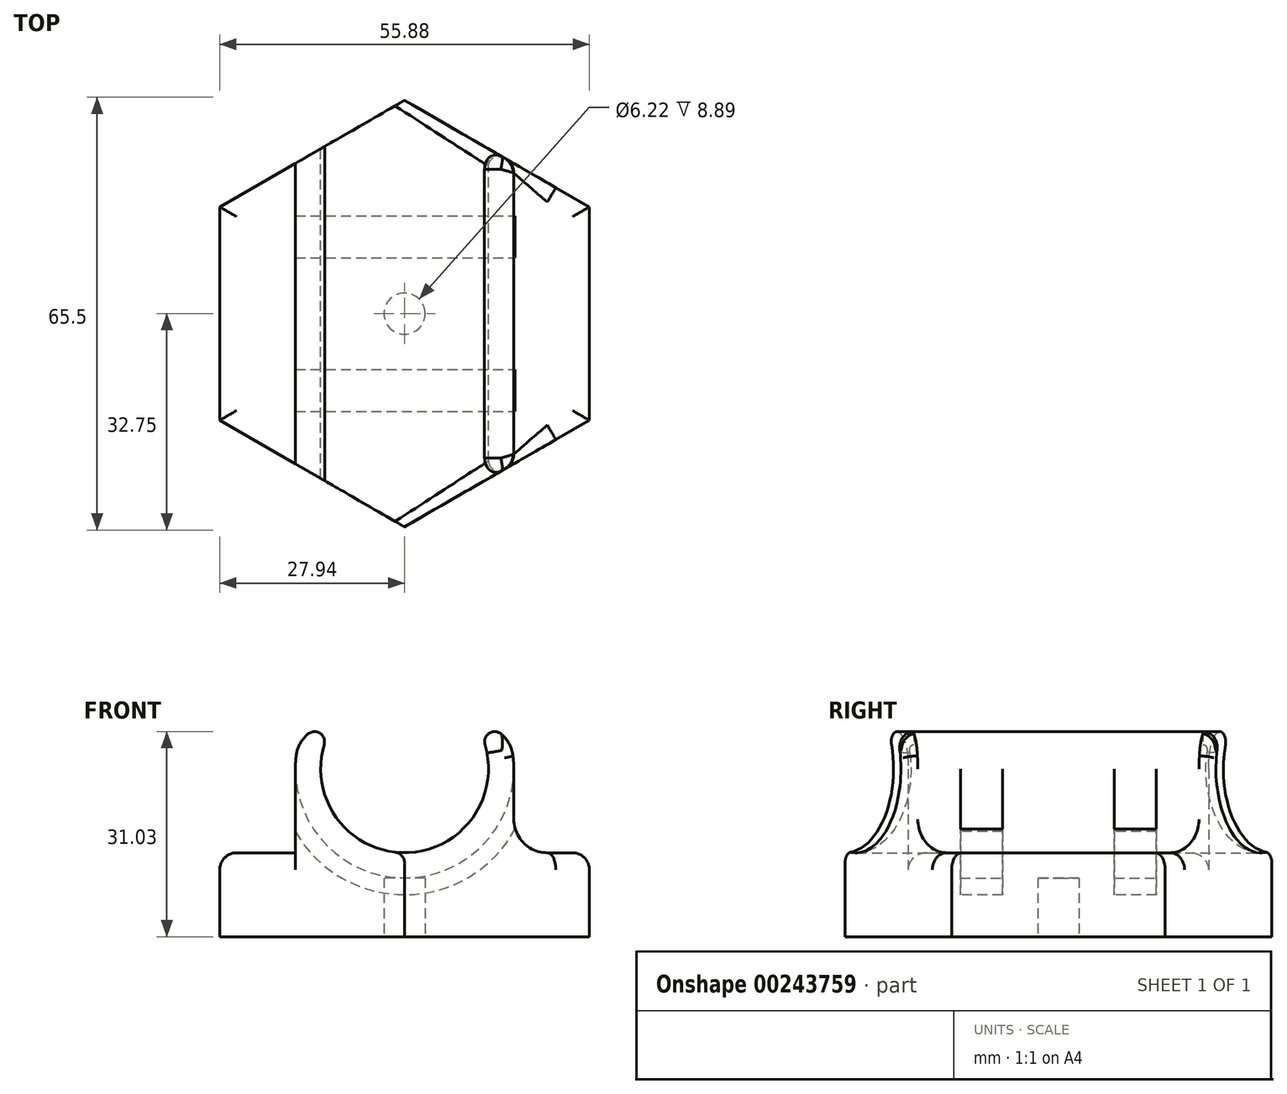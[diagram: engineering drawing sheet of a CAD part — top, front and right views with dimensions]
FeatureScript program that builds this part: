
annotation { "Feature Type Name" : "Feature", "Feature Type Description" : "" }
export const myFeature = defineFeature(function(context is Context, id is Id, definition is map)
    precondition{}
    {
        {
            var Q0;
            Q0=qCreatedBy(makeId("Top.planeOp"),FACE);
            var sketch = newSketch(context, id + "F0", { "sketchPlane" : qUnion([Q0])});
            skLineSegment(sketch, "E0", {"start": v(0, 0) * mm, "end": v(27.94, 0) * mm});
            skCircle(sketch, "E1.cCircle", {"center": v(0, 0) * mm, "radius": 27.94 * mm, "construction": true});
            skLineSegment(sketch, "E1.0", {"start": v(27.94, 16.13) * mm, "end": v(27.94, -16.13) * mm});
            skLineSegment(sketch, "E1.1", {"start": v(27.94, -16.13) * mm, "end": v(0, -32.26) * mm});
            skLineSegment(sketch, "E1.2", {"start": v(0, -32.26) * mm, "end": v(-27.94, -16.13) * mm});
            skLineSegment(sketch, "E1.3", {"start": v(-27.94, -16.13) * mm, "end": v(-27.94, 16.13) * mm});
            skLineSegment(sketch, "E1.4", {"start": v(-27.94, 16.13) * mm, "end": v(0, 32.26) * mm});
            skLineSegment(sketch, "E1.5", {"start": v(0, 32.26) * mm, "end": v(27.94, 16.13) * mm});
            skPoint(sketch, "E1.0.midPoint", {"position": v(27.94, 0) * mm});
            skCircle(sketch, "E2", {"center": v(0, 0) * mm, "radius": 3.11 * mm});
            skSolve(sketch);
        }
        {
            var Q0;
            {var subQ0=sQuery(id+"F0.wireOp",EDGE,"E1.1");Q0=makeQuery(id+"F0.imprint","IMPRINT",FACE,{"disambiguationData":[TD([[makeQuery(id+"F0.imprint","IMPRINT",EDGE,{"derivedFrom":subQ0}),-1.0]])]});}
            extrude(context, id + "F1", {"entities" : qUnion([Q0]), "depth" : 12.7 * mm});
        }
        {
            var Q0;
            Q0=qCreatedBy(makeId("Front.planeOp"),FACE);
            var sketch = newSketch(context, id + "F2", { "sketchPlane" : qUnion([Q0])});
            skLineSegment(sketch, "E3", {"start": v(0, 0) * mm, "end": v(0, 25.4) * mm});
            skCircle(sketch, "E4", {"center": v(0, 25.4) * mm, "radius": 12.7 * mm});
            skCircle(sketch, "E5", {"center": v(0, 25.4) * mm, "radius": 16.51 * mm});
            skLineSegment(sketch, "E6", {"start": v(0, 0) * mm, "end": v(0, 12.7) * mm});
            skLineSegment(sketch, "E7", {"start": v(0, 12.7) * mm, "end": v(27.94, 12.7) * mm});
            skLineSegment(sketch, "E8", {"start": v(0, 12.7) * mm, "end": v(-27.94, 12.7) * mm});
            skLineSegment(sketch, "E9", {"start": v(-16.51, 25.4) * mm, "end": v(-16.51, 12.7) * mm});
            skLineSegment(sketch, "E10", {"start": v(16.51, 25.4) * mm, "end": v(16.51, 12.7) * mm});
            skLineSegment(sketch, "E11", {"start": v(0, 25.4) * mm, "end": v(-14.24, 33.76) * mm});
            skLineSegment(sketch, "E12", {"start": v(0, 25.4) * mm, "end": v(14.24, 33.76) * mm});
            skSolve(sketch);
        }
        {
            var Q0;
            Q0=makeQuery(id+"F0.imprint","IMPRINT",FACE,{"disambiguationData":[TD([[makeQuery(id+"F0.imprint","IMPRINT",EDGE,{"derivedFrom":sQuery(id+"F0.wireOp",EDGE,"E2")}),1.0]])]});
            extrude(context, id + "F3", {"entities" : qUnion([Q0]), "operationType" : NewBodyOperationType.ADD, "depth" : 12.7 * mm, "hasSecondDirection" : true, "secondDirectionOppositeDirection" : false, "secondDirectionDepth" : 8.9 * mm});
        }
        {
            var Q0;
            {var subQ3=sQuery(id+"F2.wireOp",EDGE,"E5");var subQ5=makeQuery(id+"F2.imprint","INTERSECT",VERTEX,{"derivedFrom":[subQ3,sQuery(id+"F2.wireOp",EDGE,"E9")]});Q0=makeQuery(id+"F2.imprint","IMPRINT",FACE,{"disambiguationData":[TD([[makeQuery(id+"F2.imprint","IMPRINT",EDGE,{"disambiguationData":[TD([[subQ5,1.0]])],"derivedFrom":subQ3}),1.0]])]});}
            var Q1;
            {var subQ0=sQuery(id+"F2.wireOp",EDGE,"E9");Q1=makeQuery(id+"F2.imprint","IMPRINT",FACE,{"disambiguationData":[TD([[makeQuery(id+"F2.imprint","IMPRINT",EDGE,{"derivedFrom":subQ0}),1.0]])]});}
            var Q2;
            Q2=makeQuery(id+"F1.opExtrude","SWEPT_FACE",FACE,{"disambiguationData":[OSD([sQuery(id+"F0.wireOp",EDGE,"E1.2")])]});
            extrude(context, id + "F4", {"entities" : qUnion([Q0, Q1]), "operationType" : NewBodyOperationType.ADD, "endBound" : BoundingType.UP_TO_SURFACE, "endBoundEntityFace" : qUnion([Q2]), "depth" : 25.4 * mm});
        }
        {
            var Q0;
            {var subQ3=sQuery(id+"F2.wireOp",EDGE,"E5");var subQ5=makeQuery(id+"F2.imprint","INTERSECT",VERTEX,{"derivedFrom":[subQ3,sQuery(id+"F2.wireOp",EDGE,"E10")]});Q0=makeQuery(id+"F2.imprint","IMPRINT",FACE,{"disambiguationData":[TD([[makeQuery(id+"F2.imprint","IMPRINT",EDGE,{"disambiguationData":[TD([[subQ5,-1.0]])],"derivedFrom":subQ3}),1.0]])]});}
            var Q1;
            {var subQ0=sQuery(id+"F2.wireOp",EDGE,"E10");Q1=makeQuery(id+"F2.imprint","IMPRINT",FACE,{"disambiguationData":[TD([[makeQuery(id+"F2.imprint","IMPRINT",EDGE,{"derivedFrom":subQ0}),-1.0]])]});}
            var Q2;
            Q2=makeQuery(id+"F1.opExtrude","SWEPT_FACE",FACE,{"disambiguationData":[OSD([sQuery(id+"F0.wireOp",EDGE,"E1.1")])]});
            extrude(context, id + "F5", {"entities" : qUnion([Q0, Q1]), "operationType" : NewBodyOperationType.ADD, "endBound" : BoundingType.UP_TO_SURFACE, "endBoundEntityFace" : qUnion([Q2]), "depth" : 25.4 * mm});
        }
        {
            var Q0;
            {var subQ3=sQuery(id+"F2.wireOp",EDGE,"E5");var subQ5=makeQuery(id+"F2.imprint","INTERSECT",VERTEX,{"derivedFrom":[subQ3,sQuery(id+"F2.wireOp",EDGE,"E10")]});Q0=makeQuery(id+"F2.imprint","IMPRINT",FACE,{"disambiguationData":[TD([[makeQuery(id+"F2.imprint","IMPRINT",EDGE,{"disambiguationData":[TD([[subQ5,-1.0]])],"derivedFrom":subQ3}),1.0]])]});}
            var Q1;
            {var subQ0=sQuery(id+"F2.wireOp",EDGE,"E10");Q1=makeQuery(id+"F2.imprint","IMPRINT",FACE,{"disambiguationData":[TD([[makeQuery(id+"F2.imprint","IMPRINT",EDGE,{"derivedFrom":subQ0}),-1.0]])]});}
            var Q2;
            Q2=makeQuery(id+"F1.opExtrude","SWEPT_FACE",FACE,{"disambiguationData":[OSD([sQuery(id+"F0.wireOp",EDGE,"E1.5")])]});
            extrude(context, id + "F6", {"entities" : qUnion([Q0, Q1]), "operationType" : NewBodyOperationType.ADD, "endBound" : BoundingType.UP_TO_SURFACE, "oppositeDirection" : true, "endBoundEntityFace" : qUnion([Q2]), "depth" : 25.4 * mm});
        }
        {
            var Q0;
            {var subQ3=sQuery(id+"F2.wireOp",EDGE,"E5");var subQ5=makeQuery(id+"F2.imprint","INTERSECT",VERTEX,{"derivedFrom":[subQ3,sQuery(id+"F2.wireOp",EDGE,"E9")]});Q0=makeQuery(id+"F2.imprint","IMPRINT",FACE,{"disambiguationData":[TD([[makeQuery(id+"F2.imprint","IMPRINT",EDGE,{"disambiguationData":[TD([[subQ5,1.0]])],"derivedFrom":subQ3}),1.0]])]});}
            var Q1;
            {var subQ0=sQuery(id+"F2.wireOp",EDGE,"E9");Q1=makeQuery(id+"F2.imprint","IMPRINT",FACE,{"disambiguationData":[TD([[makeQuery(id+"F2.imprint","IMPRINT",EDGE,{"derivedFrom":subQ0}),1.0]])]});}
            var Q2;
            Q2=makeQuery(id+"F1.opExtrude","SWEPT_FACE",FACE,{"disambiguationData":[OSD([sQuery(id+"F0.wireOp",EDGE,"E1.4")])]});
            extrude(context, id + "F7", {"entities" : qUnion([Q0, Q1]), "operationType" : NewBodyOperationType.ADD, "endBound" : BoundingType.UP_TO_SURFACE, "oppositeDirection" : true, "endBoundEntityFace" : qUnion([Q2]), "depth" : 25.4 * mm});
        }
        {
            var Q0;
            {var subQ0=sQuery(id+"F2.wireOp",EDGE,"E9");var subQ1=sQuery(id+"F2.wireOp",EDGE,"E8");Q0=makeQuery(id+"F7.boolean.opBoolean","MERGE",EDGE,{"derivedFrom":[makeQuery(id+"F4.opExtrude","SWEPT_EDGE",EDGE,{"disambiguationData":[OSD([subQ1,subQ0])]}),makeQuery(id+"F7.opExtrude","SWEPT_EDGE",EDGE,{"disambiguationData":[OSD([subQ1,subQ0])]})]});}
            var Q1;
            {var subQ0=sQuery(id+"F2.wireOp",EDGE,"E10");var subQ1=sQuery(id+"F2.wireOp",EDGE,"E7");Q1=makeQuery(id+"F6.boolean.opBoolean","MERGE",EDGE,{"derivedFrom":[makeQuery(id+"F5.opExtrude","SWEPT_EDGE",EDGE,{"disambiguationData":[OSD([subQ1,subQ0])]}),makeQuery(id+"F6.opExtrude","SWEPT_EDGE",EDGE,{"disambiguationData":[OSD([subQ1,subQ0])]})]});}
            fillet(context, id + "F8", {"entities" : qUnion([Q0, Q1]), "radius" : 5.08 * mm, "tangentPropagation" : true, "allowEdgeOverflow" : false});
        }
        {
            var Q0;
            {var subQ0=sQuery(id+"F2.wireOp",EDGE,"E11");var subQ1=sQuery(id+"F2.wireOp",EDGE,"E5");Q0=makeQuery(id+"F7.boolean.opBoolean","MERGE",EDGE,{"derivedFrom":[makeQuery(id+"F4.opExtrude","SWEPT_EDGE",EDGE,{"disambiguationData":[OSD([subQ1,subQ0])]}),makeQuery(id+"F7.opExtrude","SWEPT_EDGE",EDGE,{"disambiguationData":[OSD([subQ1,subQ0])]})]});}
            var Q1;
            {var subQ0=sQuery(id+"F2.wireOp",EDGE,"E12");var subQ1=sQuery(id+"F2.wireOp",EDGE,"E5");Q1=makeQuery(id+"F6.boolean.opBoolean","MERGE",EDGE,{"derivedFrom":[makeQuery(id+"F5.opExtrude","SWEPT_EDGE",EDGE,{"disambiguationData":[OSD([subQ1,subQ0])]}),makeQuery(id+"F6.opExtrude","SWEPT_EDGE",EDGE,{"disambiguationData":[OSD([subQ1,subQ0])]})]});}
            fillet(context, id + "F9", {"entities" : qUnion([Q0, Q1]), "radius" : 5.08 * mm, "tangentPropagation" : true, "allowEdgeOverflow" : false});
        }
        {
            var Q0;
            Q0=makeQuery(id+"F1.opExtrude","CAP_EDGE",EDGE,{"disambiguationData":[OSD([sQuery(id+"F0.wireOp",EDGE,"E1.4")])],"isStart":false});
            var Q1;
            Q1=makeQuery(id+"F1.opExtrude","CAP_EDGE",EDGE,{"disambiguationData":[OSD([sQuery(id+"F0.wireOp",EDGE,"E1.3")])],"isStart":false});
            var Q2;
            Q2=makeQuery(id+"F1.opExtrude","CAP_EDGE",EDGE,{"disambiguationData":[OSD([sQuery(id+"F0.wireOp",EDGE,"E1.2")])],"isStart":false});
            var Q3;
            Q3=makeQuery(id+"F1.opExtrude","CAP_EDGE",EDGE,{"disambiguationData":[OSD([sQuery(id+"F0.wireOp",EDGE,"E1.1")])],"isStart":false});
            var Q4;
            Q4=makeQuery(id+"F1.opExtrude","CAP_EDGE",EDGE,{"disambiguationData":[OSD([sQuery(id+"F0.wireOp",EDGE,"E1.0")])],"isStart":false});
            var Q5;
            Q5=makeQuery(id+"F1.opExtrude","CAP_EDGE",EDGE,{"disambiguationData":[OSD([sQuery(id+"F0.wireOp",EDGE,"E1.5")])],"isStart":false});
            fillet(context, id + "F10", {"entities" : qUnion([Q0, Q1, Q2, Q3, Q4, Q5]), "radius" : 2.54 * mm, "tangentPropagation" : true, "allowEdgeOverflow" : false});
        }
        {
            var Q0;
            Q0=qCreatedBy(makeId("Right.planeOp"),FACE);
            var sketch = newSketch(context, id + "F11", { "sketchPlane" : qUnion([Q0])});
            skLineSegment(sketch, "E13", {"start": v(0, 0) * mm, "end": v(0, 41.91) * mm});
            skLineSegment(sketch, "E14", {"start": v(-11.63, 41.91) * mm, "end": v(-8.46, 41.91) * mm});
            skLineSegment(sketch, "E15", {"start": v(-8.46, 41.91) * mm, "end": v(-8.46, 44.45) * mm});
            skLineSegment(sketch, "E16", {"start": v(-8.46, 44.45) * mm, "end": v(-14.8, 44.45) * mm});
            skLineSegment(sketch, "E17", {"start": v(-14.8, 44.45) * mm, "end": v(-14.8, 41.91) * mm});
            skLineSegment(sketch, "E18", {"start": v(-14.8, 41.91) * mm, "end": v(-11.63, 41.91) * mm});
            skLineSegment(sketch, "E19.MirrorCS", {"start": v(8.46, 41.91) * mm, "end": v(8.46, 44.45) * mm});
            skLineSegment(sketch, "E20.MirrorCS", {"start": v(11.63, 41.91) * mm, "end": v(8.46, 41.91) * mm});
            skLineSegment(sketch, "E21.MirrorCS", {"start": v(8.46, 44.45) * mm, "end": v(14.8, 44.45) * mm});
            skLineSegment(sketch, "E22.MirrorCS", {"start": v(14.8, 41.91) * mm, "end": v(11.63, 41.91) * mm});
            skLineSegment(sketch, "E23.MirrorCS", {"start": v(14.8, 44.45) * mm, "end": v(14.8, 41.91) * mm});
            skSolve(sketch);
        }
        {
            var Q0;
            Q0=makeQuery(id+"F11.imprint","IMPRINT",FACE,{"disambiguationData":[TD([[makeQuery(id+"F11.imprint","IMPRINT",EDGE,{"derivedFrom":sQuery(id+"F11.wireOp",EDGE,"E14")}),1.0]])]});
            var Q1;
            Q1=makeQuery(id+"F11.imprint","IMPRINT",FACE,{"disambiguationData":[TD([[makeQuery(id+"F11.imprint","IMPRINT",EDGE,{"derivedFrom":sQuery(id+"F11.wireOp",EDGE,"E19.MirrorCS")}),-1.0]])]});
            var Q2;
            Q2=sQuery(id+"F2.wireOp",EDGE,"E5");
            sweep(context, id + "F12", {"operationType" : NewBodyOperationType.REMOVE, "profiles" : qUnion([Q0, Q1]), "path" : qUnion([Q2])});
        }
        {
            var Q0;
            {var subQ0=sQuery(id+"F2.wireOp",EDGE,"E4");var subQ1=sQuery(id+"F2.wireOp",EDGE,"E11");var subQ2=sQuery(id+"F2.wireOp",EDGE,"E5");Q0=makeQuery(id+"F9.opFillet","BLEND_EDGE",EDGE,{"blendedFrom":[makeQuery(id+"F7.boolean.opBoolean","MERGE",EDGE,{"derivedFrom":[makeQuery(id+"F4.opExtrude","SWEPT_EDGE",EDGE,{"disambiguationData":[OSD([subQ2,subQ1])]}),makeQuery(id+"F7.opExtrude","SWEPT_EDGE",EDGE,{"disambiguationData":[OSD([subQ2,subQ1])]})]}),makeQuery(id+"F7.boolean.opBoolean","MERGE",FACE,{"derivedFrom":[makeQuery(id+"F6.boolean.opBoolean","MERGE",FACE,{"derivedFrom":[makeQuery(id+"F5.boolean.opBoolean","MERGE",FACE,{"derivedFrom":[makeQuery(id+"F4.opExtrude","SWEPT_FACE",FACE,{"disambiguationData":[OSD([subQ0])]}),makeQuery(id+"F5.opExtrude","SWEPT_FACE",FACE,{"disambiguationData":[OSD([subQ0])]})]}),makeQuery(id+"F6.opExtrude","SWEPT_FACE",FACE,{"disambiguationData":[OSD([subQ0])]})]}),makeQuery(id+"F7.opExtrude","SWEPT_FACE",FACE,{"disambiguationData":[OSD([subQ0])]})]})],"blendedInto":[makeQuery(id+"F7.boolean.opBoolean","MERGE",FACE,{"derivedFrom":[makeQuery(id+"F6.boolean.opBoolean","MERGE",FACE,{"derivedFrom":[makeQuery(id+"F5.boolean.opBoolean","MERGE",FACE,{"derivedFrom":[makeQuery(id+"F4.opExtrude","SWEPT_FACE",FACE,{"disambiguationData":[OSD([subQ0])]}),makeQuery(id+"F5.opExtrude","SWEPT_FACE",FACE,{"disambiguationData":[OSD([subQ0])]})]}),makeQuery(id+"F6.opExtrude","SWEPT_FACE",FACE,{"disambiguationData":[OSD([subQ0])]})]}),makeQuery(id+"F7.opExtrude","SWEPT_FACE",FACE,{"disambiguationData":[OSD([subQ0])]})]})]});}
            var Q1;
            {var subQ0=sQuery(id+"F2.wireOp",EDGE,"E4");var subQ1=sQuery(id+"F2.wireOp",EDGE,"E12");var subQ2=sQuery(id+"F2.wireOp",EDGE,"E5");Q1=makeQuery(id+"F9.opFillet","BLEND_EDGE",EDGE,{"blendedFrom":[makeQuery(id+"F6.boolean.opBoolean","MERGE",EDGE,{"derivedFrom":[makeQuery(id+"F5.opExtrude","SWEPT_EDGE",EDGE,{"disambiguationData":[OSD([subQ2,subQ1])]}),makeQuery(id+"F6.opExtrude","SWEPT_EDGE",EDGE,{"disambiguationData":[OSD([subQ2,subQ1])]})]}),makeQuery(id+"F7.boolean.opBoolean","MERGE",FACE,{"derivedFrom":[makeQuery(id+"F6.boolean.opBoolean","MERGE",FACE,{"derivedFrom":[makeQuery(id+"F5.boolean.opBoolean","MERGE",FACE,{"derivedFrom":[makeQuery(id+"F4.opExtrude","SWEPT_FACE",FACE,{"disambiguationData":[OSD([subQ0])]}),makeQuery(id+"F5.opExtrude","SWEPT_FACE",FACE,{"disambiguationData":[OSD([subQ0])]})]}),makeQuery(id+"F6.opExtrude","SWEPT_FACE",FACE,{"disambiguationData":[OSD([subQ0])]})]}),makeQuery(id+"F7.opExtrude","SWEPT_FACE",FACE,{"disambiguationData":[OSD([subQ0])]})]})],"blendedInto":[makeQuery(id+"F7.boolean.opBoolean","MERGE",FACE,{"derivedFrom":[makeQuery(id+"F6.boolean.opBoolean","MERGE",FACE,{"derivedFrom":[makeQuery(id+"F5.boolean.opBoolean","MERGE",FACE,{"derivedFrom":[makeQuery(id+"F4.opExtrude","SWEPT_FACE",FACE,{"disambiguationData":[OSD([subQ0])]}),makeQuery(id+"F5.opExtrude","SWEPT_FACE",FACE,{"disambiguationData":[OSD([subQ0])]})]}),makeQuery(id+"F6.opExtrude","SWEPT_FACE",FACE,{"disambiguationData":[OSD([subQ0])]})]}),makeQuery(id+"F7.opExtrude","SWEPT_FACE",FACE,{"disambiguationData":[OSD([subQ0])]})]})]});}
            fillet(context, id + "F13", {"entities" : qUnion([Q0, Q1]), "radius" : 1.52 * mm, "tangentPropagation" : true, "allowEdgeOverflow" : false});
        }
    });
